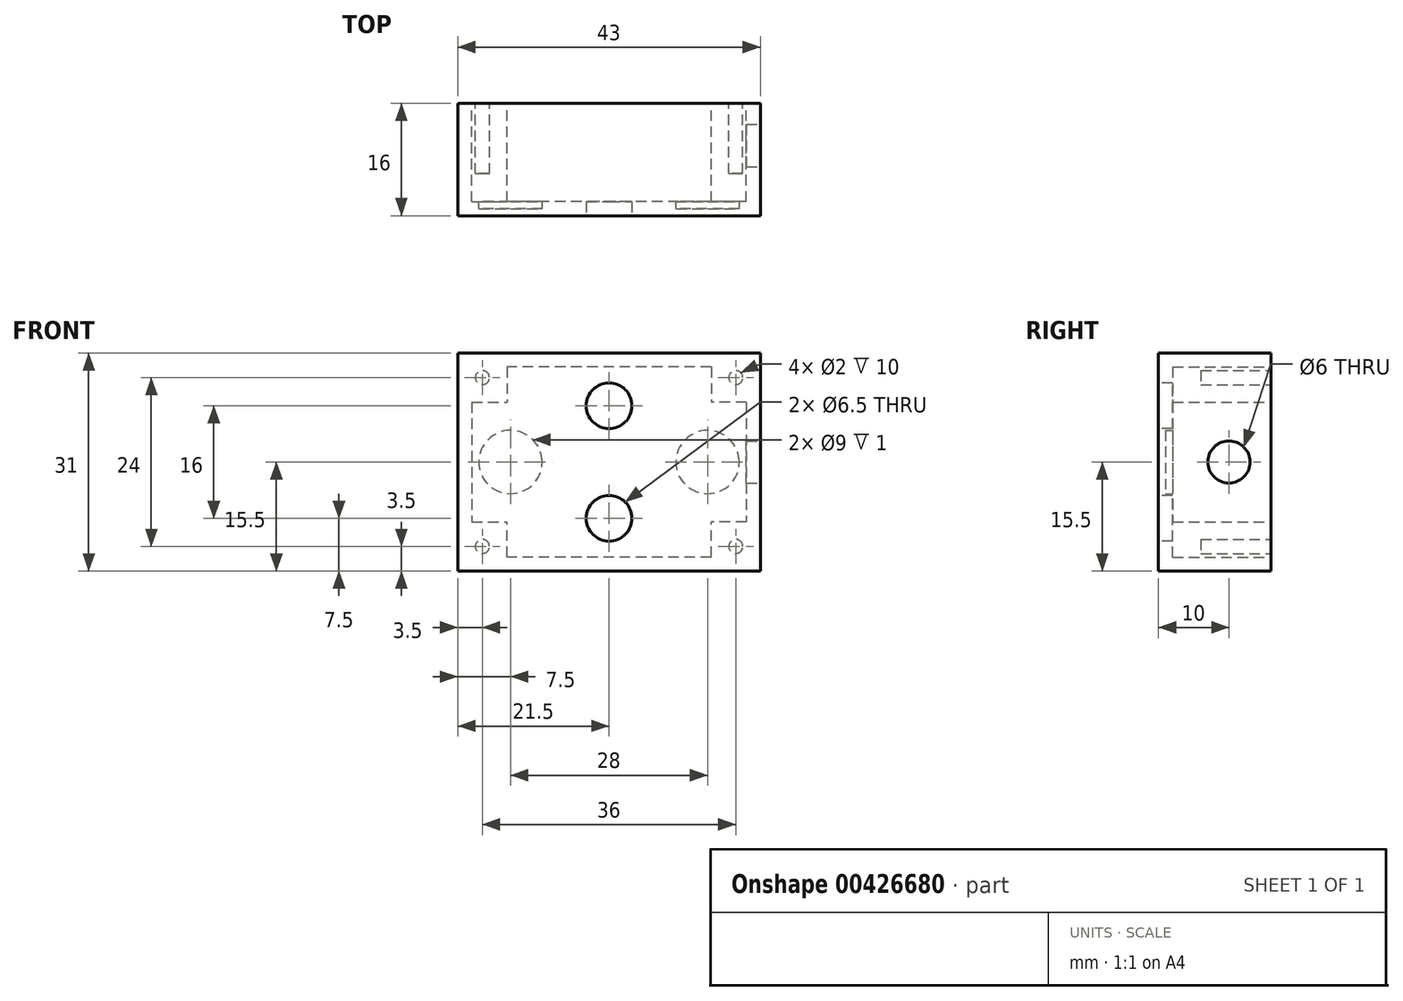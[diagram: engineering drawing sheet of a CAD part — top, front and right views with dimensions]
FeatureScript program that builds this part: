
annotation { "Feature Type Name" : "Feature", "Feature Type Description" : "" }
export const myFeature = defineFeature(function(context is Context, id is Id, definition is map)
    precondition{}
    {
        {
            var Q0;
            Q0=qCreatedBy(makeId("Front.planeOp"),FACE);
            var sketch = newSketch(context, id + "F0", { "sketchPlane" : qUnion([Q0])});
            skLineSegment(sketch, "E0.bottom", {"start": v(21.5, 15.5) * mm, "end": v(-21.5, 15.5) * mm});
            skLineSegment(sketch, "E0.top", {"start": v(21.5, -15.5) * mm, "end": v(-21.5, -15.5) * mm});
            skLineSegment(sketch, "E0.left", {"start": v(21.5, 15.5) * mm, "end": v(21.5, -15.5) * mm});
            skLineSegment(sketch, "E0.right", {"start": v(-21.5, 15.5) * mm, "end": v(-21.5, -15.5) * mm});
            skPoint(sketch, "E0.middle", {"position": v(0, 0) * mm});
            skSolve(sketch);
        }
        {
            var Q0;
            Q0 = qSketchRegion(id + "F0", true);
            extrude(context, id + "F1", {"entities" : qUnion([Q0]), "depth" : 16 * mm});
        }
        {
            var Q0;
            Q0=makeQuery(id+"F1.opExtrude","CAP_FACE",FACE,{"disambiguationData":[OSD([sQuery(id+"F0.wireOp",EDGE,"E0.bottom"),sQuery(id+"F0.wireOp",EDGE,"E0.top"),sQuery(id+"F0.wireOp",EDGE,"E0.left"),sQuery(id+"F0.wireOp",EDGE,"E0.right")])],"isStart":true});
            shell(context, id + "F2", {"entities" : qUnion([Q0]), "thickness" : 2 * mm});
        }
        {
            var Q0;
            Q0=makeQuery(id+"F1.opExtrude","CAP_FACE",FACE,{"disambiguationData":[OSD([sQuery(id+"F0.wireOp",EDGE,"E0.bottom"),sQuery(id+"F0.wireOp",EDGE,"E0.top"),sQuery(id+"F0.wireOp",EDGE,"E0.left"),sQuery(id+"F0.wireOp",EDGE,"E0.right")])],"isStart":false});
            var sketch = newSketch(context, id + "F3", { "sketchPlane" : qUnion([Q0])});
            skCircle(sketch, "E1", {"center": v(0, 8) * mm, "radius": 3.25 * mm});
            skCircle(sketch, "E2", {"center": v(0, -8) * mm, "radius": 3.25 * mm});
            skSolve(sketch);
        }
        {
            var Q0;
            Q0 = qSketchRegion(id + "F3", true);
            extrude(context, id + "F4", {"entities" : qUnion([Q0]), "operationType" : NewBodyOperationType.REMOVE, "endBound" : BoundingType.THROUGH_ALL, "oppositeDirection" : true, "depth" : 25 * mm});
        }
        {
            var Q0;
            Q0=makeQuery(id+"F1.opExtrude","SWEPT_FACE",FACE,{"disambiguationData":[OSD([sQuery(id+"F0.wireOp",EDGE,"E0.left")])]});
            var sketch = newSketch(context, id + "F5", { "sketchPlane" : qUnion([Q0])});
            skCircle(sketch, "E3", {"center": v(-6, 0) * mm, "radius": 3 * mm});
            skSolve(sketch);
        }
        {
            var Q0;
            Q0=makeQuery(id+"F5.imprint","IMPRINT",FACE,{"disambiguationData":[TD([[makeQuery(id+"F5.imprint","IMPRINT",EDGE,{"derivedFrom":sQuery(id+"F5.wireOp",EDGE,"E3")}),1.0]])]});
            extrude(context, id + "F6", {"entities" : qUnion([Q0]), "operationType" : NewBodyOperationType.REMOVE, "oppositeDirection" : true, "depth" : 7.6 * mm});
        }
        {
            var Q0;
            Q0=makeQuery(id+"F1.opExtrude","CAP_FACE",FACE,{"disambiguationData":[OSD([sQuery(id+"F0.wireOp",EDGE,"E0.bottom"),sQuery(id+"F0.wireOp",EDGE,"E0.top"),sQuery(id+"F0.wireOp",EDGE,"E0.left"),sQuery(id+"F0.wireOp",EDGE,"E0.right")])],"isStart":true});
            var sketch = newSketch(context, id + "F7", { "sketchPlane" : qUnion([Q0])});
            skLineSegment(sketch, "E4.bottom", {"start": v(19.5, 13.5) * mm, "end": v(14.5, 13.5) * mm});
            skLineSegment(sketch, "E4.top", {"start": v(19.5, 8.5) * mm, "end": v(14.5, 8.5) * mm});
            skLineSegment(sketch, "E4.left", {"start": v(19.5, 13.5) * mm, "end": v(19.5, 8.5) * mm});
            skLineSegment(sketch, "E4.right", {"start": v(14.5, 13.5) * mm, "end": v(14.5, 8.5) * mm});
            skSolve(sketch);
        }
        {
            var Q0;
            Q0 = qSketchRegion(id + "F7", true);
            extrude(context, id + "F8", {"entities" : qUnion([Q0]), "operationType" : NewBodyOperationType.ADD, "endBound" : BoundingType.UP_TO_NEXT, "oppositeDirection" : true, "depth" : 25 * mm});
        }
        {
            var Q0;
            Q0=makeQuery(id+"F8.boolean.opBoolean","MERGE",FACE,{"derivedFrom":[makeQuery(id+"F1.opExtrude","CAP_FACE",FACE,{"disambiguationData":[OSD([sQuery(id+"F0.wireOp",EDGE,"E0.bottom"),sQuery(id+"F0.wireOp",EDGE,"E0.top"),sQuery(id+"F0.wireOp",EDGE,"E0.left"),sQuery(id+"F0.wireOp",EDGE,"E0.right")])],"isStart":true}),makeQuery(id+"F8.opExtrude","CAP_FACE",FACE,{"disambiguationData":[OSD([sQuery(id+"F7.wireOp",EDGE,"E4.bottom"),sQuery(id+"F7.wireOp",EDGE,"E4.top"),sQuery(id+"F7.wireOp",EDGE,"E4.left"),sQuery(id+"F7.wireOp",EDGE,"E4.right")])],"isStart":true})]});
            var sketch = newSketch(context, id + "F9", { "sketchPlane" : qUnion([Q0])});
            skLineSegment(sketch, "E5.bottom", {"start": v(19.5, -13.5) * mm, "end": v(14.5, -13.5) * mm});
            skLineSegment(sketch, "E5.top", {"start": v(19.5, -8.5) * mm, "end": v(14.5, -8.5) * mm});
            skLineSegment(sketch, "E5.left", {"start": v(19.5, -13.5) * mm, "end": v(19.5, -8.5) * mm});
            skLineSegment(sketch, "E5.right", {"start": v(14.5, -13.5) * mm, "end": v(14.5, -8.5) * mm});
            skLineSegment(sketch, "E6.bottom", {"start": v(-19.5, -13.5) * mm, "end": v(-14.5, -13.5) * mm});
            skLineSegment(sketch, "E6.top", {"start": v(-19.5, -8.5) * mm, "end": v(-14.5, -8.5) * mm});
            skLineSegment(sketch, "E6.left", {"start": v(-19.5, -13.5) * mm, "end": v(-19.5, -8.5) * mm});
            skLineSegment(sketch, "E6.right", {"start": v(-14.5, -13.5) * mm, "end": v(-14.5, -8.5) * mm});
            skLineSegment(sketch, "E7.bottom", {"start": v(-19.5, 13.5) * mm, "end": v(-14.5, 13.5) * mm});
            skLineSegment(sketch, "E7.top", {"start": v(-19.5, 8.5) * mm, "end": v(-14.5, 8.5) * mm});
            skLineSegment(sketch, "E7.left", {"start": v(-19.5, 13.5) * mm, "end": v(-19.5, 8.5) * mm});
            skLineSegment(sketch, "E7.right", {"start": v(-14.5, 13.5) * mm, "end": v(-14.5, 8.5) * mm});
            skSolve(sketch);
        }
        {
            var Q0;
            Q0 = qSketchRegion(id + "F9", true);
            extrude(context, id + "F10", {"entities" : qUnion([Q0]), "endBound" : BoundingType.UP_TO_NEXT, "oppositeDirection" : true, "depth" : 25 * mm});
        }
        {
            var Q0;
            Q0=makeQuery(id+"F1.opExtrude","SWEPT_BODY",BODY,{"disambiguationData":[OSD([sQuery(id+"F0.wireOp",EDGE,"E0.bottom"),sQuery(id+"F0.wireOp",EDGE,"E0.top"),sQuery(id+"F0.wireOp",EDGE,"E0.left"),sQuery(id+"F0.wireOp",EDGE,"E0.right")])]});
            var Q1;
            Q1=makeQuery(id+"F10.opExtrude","SWEPT_BODY",BODY,{"disambiguationData":[OSD([sQuery(id+"F9.wireOp",EDGE,"E5.bottom"),sQuery(id+"F9.wireOp",EDGE,"E5.top"),sQuery(id+"F9.wireOp",EDGE,"E5.left"),sQuery(id+"F9.wireOp",EDGE,"E5.right")])]});
            var Q2;
            Q2=makeQuery(id+"F10.opExtrude","SWEPT_BODY",BODY,{"disambiguationData":[OSD([sQuery(id+"F9.wireOp",EDGE,"E6.bottom"),sQuery(id+"F9.wireOp",EDGE,"E6.top"),sQuery(id+"F9.wireOp",EDGE,"E6.left"),sQuery(id+"F9.wireOp",EDGE,"E6.right")])]});
            var Q3;
            Q3=makeQuery(id+"F10.opExtrude","SWEPT_BODY",BODY,{"disambiguationData":[OSD([sQuery(id+"F9.wireOp",EDGE,"E7.bottom"),sQuery(id+"F9.wireOp",EDGE,"E7.top"),sQuery(id+"F9.wireOp",EDGE,"E7.left"),sQuery(id+"F9.wireOp",EDGE,"E7.right")])]});
            booleanBodies(context, id + "F11", {"operationType" : BooleanOperationType.UNION, "tools" : qUnion([Q0, Q1, Q2, Q3])});
        }
        {
            var Q0;
            Q0=makeQuery(id+"F11.opBoolean","MERGE",FACE,{"derivedFrom":[makeQuery(id+"F8.boolean.opBoolean","MERGE",FACE,{"derivedFrom":[makeQuery(id+"F1.opExtrude","CAP_FACE",FACE,{"disambiguationData":[OSD([sQuery(id+"F0.wireOp",EDGE,"E0.bottom"),sQuery(id+"F0.wireOp",EDGE,"E0.top"),sQuery(id+"F0.wireOp",EDGE,"E0.left"),sQuery(id+"F0.wireOp",EDGE,"E0.right")])],"isStart":true}),makeQuery(id+"F8.opExtrude","CAP_FACE",FACE,{"disambiguationData":[OSD([sQuery(id+"F7.wireOp",EDGE,"E4.bottom"),sQuery(id+"F7.wireOp",EDGE,"E4.top"),sQuery(id+"F7.wireOp",EDGE,"E4.left"),sQuery(id+"F7.wireOp",EDGE,"E4.right")])],"isStart":true})]}),makeQuery(id+"F10.opExtrude","CAP_FACE",FACE,{"disambiguationData":[OSD([sQuery(id+"F9.wireOp",EDGE,"E5.bottom"),sQuery(id+"F9.wireOp",EDGE,"E5.top"),sQuery(id+"F9.wireOp",EDGE,"E5.left"),sQuery(id+"F9.wireOp",EDGE,"E5.right")])],"isStart":true}),makeQuery(id+"F10.opExtrude","CAP_FACE",FACE,{"disambiguationData":[OSD([sQuery(id+"F9.wireOp",EDGE,"E6.bottom"),sQuery(id+"F9.wireOp",EDGE,"E6.top"),sQuery(id+"F9.wireOp",EDGE,"E6.left"),sQuery(id+"F9.wireOp",EDGE,"E6.right")])],"isStart":true}),makeQuery(id+"F10.opExtrude","CAP_FACE",FACE,{"disambiguationData":[OSD([sQuery(id+"F9.wireOp",EDGE,"E7.bottom"),sQuery(id+"F9.wireOp",EDGE,"E7.top"),sQuery(id+"F9.wireOp",EDGE,"E7.left"),sQuery(id+"F9.wireOp",EDGE,"E7.right")])],"isStart":true})]});
            var sketch = newSketch(context, id + "F12", { "sketchPlane" : qUnion([Q0])});
            skLineSegment(sketch, "E8", {"start": v(14.5, 8.5) * mm, "end": v(21.5, 15.5) * mm, "construction": true});
            skCircle(sketch, "E9", {"center": v(18, 12) * mm, "radius": 1 * mm});
            skLineSegment(sketch, "E10", {"start": v(14.5, -8.5) * mm, "end": v(21.5, -15.5) * mm, "construction": true});
            skLineSegment(sketch, "E11", {"start": v(-14.5, -8.5) * mm, "end": v(-21.5, -15.5) * mm, "construction": true});
            skLineSegment(sketch, "E12", {"start": v(-14.5, 8.5) * mm, "end": v(-21.5, 15.5) * mm, "construction": true});
            skCircle(sketch, "E13", {"center": v(18, -12) * mm, "radius": 1 * mm});
            skCircle(sketch, "E14", {"center": v(-18, 12) * mm, "radius": 1 * mm});
            skCircle(sketch, "E15", {"center": v(-18, -12) * mm, "radius": 1 * mm});
            skSolve(sketch);
        }
        {
            var Q0;
            Q0 = qSketchRegion(id + "F12", true);
            extrude(context, id + "F13", {"entities" : qUnion([Q0]), "operationType" : NewBodyOperationType.REMOVE, "oppositeDirection" : true, "depth" : 10 * mm});
        }
        {
            var Q0;
            Q0=makeQuery(id+"F2.opShell","OFFSET_FACE",FACE,{"disambiguationData":[OSD([sQuery(id+"F0.wireOp",EDGE,"E0.bottom"),sQuery(id+"F0.wireOp",EDGE,"E0.top"),sQuery(id+"F0.wireOp",EDGE,"E0.left"),sQuery(id+"F0.wireOp",EDGE,"E0.right")])]});
            var sketch = newSketch(context, id + "F14", { "sketchPlane" : qUnion([Q0])});
            skCircle(sketch, "E16", {"center": v(-14, 0) * mm, "radius": 4.5 * mm});
            skLineSegment(sketch, "E17", {"start": v(0, 0) * mm, "end": v(0, 8.94) * mm, "construction": true});
            skCircle(sketch, "E18.MirrorC", {"center": v(14, 0) * mm, "radius": 4.5 * mm});
            skSolve(sketch);
        }
        {
            var Q0;
            Q0 = qSketchRegion(id + "F14", true);
            extrude(context, id + "F15", {"entities" : qUnion([Q0]), "operationType" : NewBodyOperationType.REMOVE, "oppositeDirection" : true, "depth" : 1 * mm});
        }
    });
